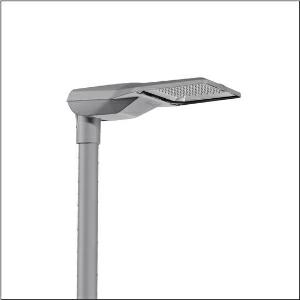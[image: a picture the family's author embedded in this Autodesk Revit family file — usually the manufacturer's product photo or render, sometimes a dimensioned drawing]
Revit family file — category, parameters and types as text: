
# Revit family: streetlight_sl_21_midi___st1_5a_5xe7p43a08mb_d510
name_source: partatom
category: Lighting Fixtures
units: mm (PartAtom-declared; Revit-internal decimal feet)

## family parameters
Cut with Voids When Loaded = No
Host = Face
Light Source = No
Part Type = Normal
Room Calculation Point = No
Round Connector Dimension = Use Diameter
Shared = No

## types (1)
- --- (1 x LED, 19830 lm, 147 W, 4000K)
    Apparent Load = 147 VA
    CIE Flux Codes = 22 53 95 100 100
    Color Rendering = 70
    Color Temperature = 4000K
    Default Elevation = 1800 mm
    Description = Streetlight SL 21 midi, mast luminaire, primary light control with lens, of PMMA, primary optical cover: cover, of toughened safety glass, transparent, light distribution: ST1.5a, light emission: direct distribution, primary light characteristic: asymmetric, installation type: post-top, side-entry, LED, 3G 1.5mm², High Power LED, rated luminous flux: 19.830lm, luminous efficacy: 135lm/W, light colour: 740, colour temperature: 4000K, control: overheat protection, constant luminous flux control, time-dependent luminous flux control, flexible luminous flux parameterisation, mains connection: 220..240V, AC, 50/60Hz, connection cable pre-assembled, cable length: 12,5m, wiring characteristics: H07RN-F, start of lifetime: 147W, end of service life: 155W, reduction: 64W, luminaire housing, of diecast aluminium, powder-coated, Siteco® metallic grey (DB 702S), corrosivity category C5 mid according to DIN EN ISO 12944, please order mast flange separately, inclination adjustable: 0°, 5°, 10°, 15°, sealing non-destructively replaceable, multi-level sealing system, length: 644mm, width: 335mm, height: 110mm, mast flange for spigot size: 42mm (side-entry): 5XC10008XM4, 60/48mm (side-entry/post-top): 5XC10108XM2, 76/60mm (side-entry/post-top): 5XC10108XM1, protection rating (complete): IP66, insulation class (complete): insulation class II (safety insulation), certification: CE, ENEC, ENEC+, VDE, impact resistance: IK09, permissible operating ambient temperature for outdoor applications: -40..+50°C, standard-compliant lighting for roads and squares, packaging unit: 1 piece

Light Distribution: ST1.5a
    Height = 111 mm
    Lamp = 1 x LED
    Lamp Light Flux = 19830 lm
    Lamp Power = 147 W
    Lamp count = 1
    Length = 644 mm
    Luminous efficacy = 135 lm/W
    Manufacturer = Siteco
    ModVariant = No
    Model = 5XE7P43A08MB
    Number of Poles = 1
    OnlyDefault = Yes
    Power Factor = 1
    Product Name = Streetlight SL 21 midi | ST1.5a
    Product group = mast luminaire | pylon top
    ProductGroupID = 6100
    Protection Class = Protection class II
    Protection Degree = IP 66
    RLX_Detail_Level = 1
    RLX_Emergency_Light_Flux = 0 lm
    RLX_Emergency_Type = 0
    RLX_Emergency_Type_DB = No
    RlxData = <blob elided: 94317 chars, md5=f45d87b5>
    Socket = socket
    Standby Power = 0 W
    System Light Flux = 19830 lm
    System Power = 147 W
    Type Comments = factory setting: luminous flux: 100 % | Output Level: 100 % | 750 mA
    Type Image = l_1004298.jpg
    URL = http://relux.com
    VarID = @adj_126915
    Voltage = 0 V
    Weight = 0.00 kg
    Width = 336 mm

## geometry (parser evidence)
native form markers: Blend x4, Sweep x10
no freeform markers — native parametric forms only
